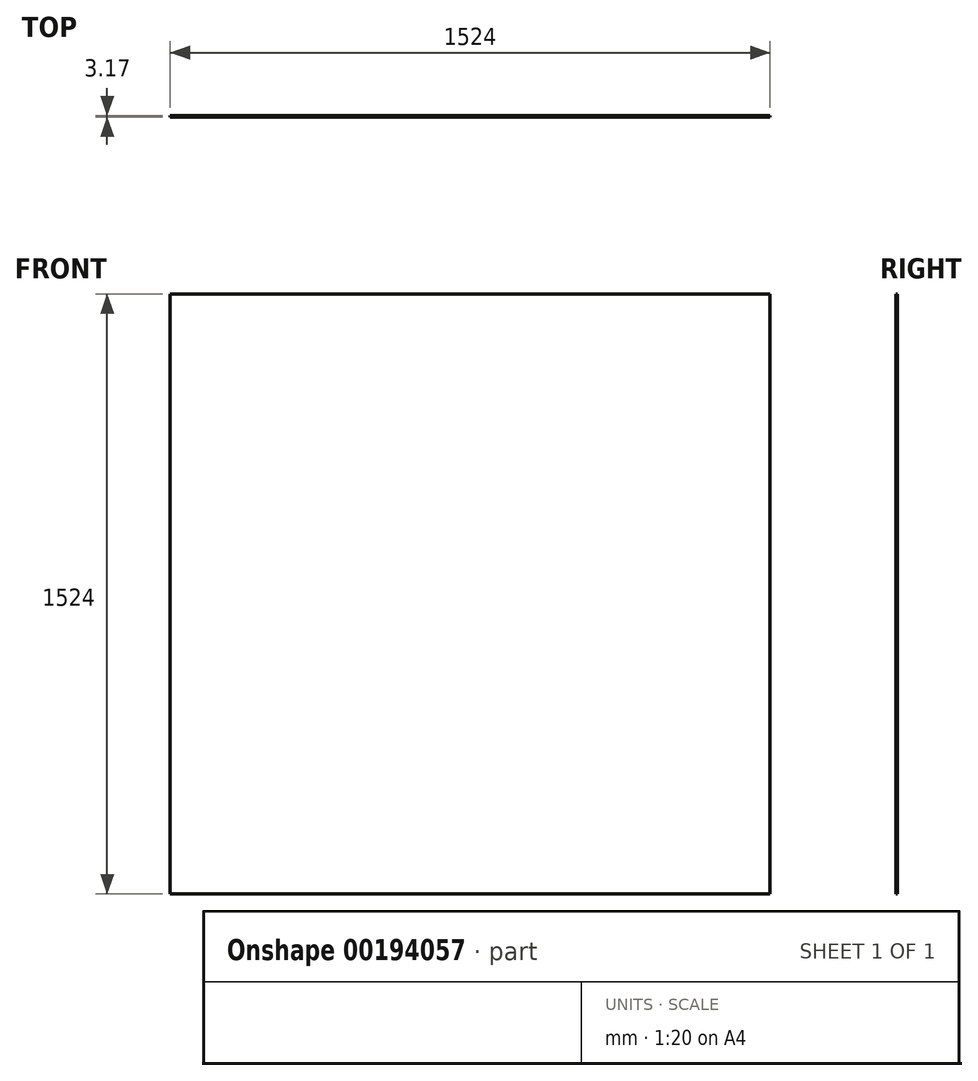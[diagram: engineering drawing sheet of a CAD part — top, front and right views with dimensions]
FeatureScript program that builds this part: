
annotation { "Feature Type Name" : "Feature", "Feature Type Description" : "" }
export const myFeature = defineFeature(function(context is Context, id is Id, definition is map)
    precondition{}
    {
        {
            var Q0;
            Q0=qCreatedBy(makeId("Front.planeOp"),FACE);
            var sketch = newSketch(context, id + "F0", { "sketchPlane" : qUnion([Q0])});
            skLineSegment(sketch, "E0.bottom", {"start": v(-825.5, 825.5) * mm, "end": v(825.5, 825.5) * mm});
            skLineSegment(sketch, "E0.top", {"start": v(-825.5, -825.5) * mm, "end": v(825.5, -825.5) * mm});
            skLineSegment(sketch, "E0.left", {"start": v(-825.5, 825.5) * mm, "end": v(-825.5, -825.5) * mm});
            skLineSegment(sketch, "E0.right", {"start": v(825.5, 825.5) * mm, "end": v(825.5, -825.5) * mm});
            skPoint(sketch, "E0.middle", {"position": v(0, 0) * mm});
            skSolve(sketch);
        }
        {
            var Q0;
            Q0=makeQuery(id+"F0.imprint","IMPRINT",FACE,{"disambiguationData":[TD([[makeQuery(id+"F0.imprint","IMPRINT",EDGE,{"derivedFrom":sQuery(id+"F0.wireOp",EDGE,"E0.bottom")}),-1.0]])]});
            extrude(context, id + "F1", {"entities" : qUnion([Q0]), "depth" : 3.17 * mm});
        }
        {
            var Q0;
            Q0=makeQuery(id+"F1.opExtrude","SWEPT_BODY",BODY,{"disambiguationData":[OSD([sQuery(id+"F0.wireOp",EDGE,"E0.bottom"),sQuery(id+"F0.wireOp",EDGE,"E0.top"),sQuery(id+"F0.wireOp",EDGE,"E0.left"),sQuery(id+"F0.wireOp",EDGE,"E0.right")])]});
            deleteBodies(context, id + "F2", {"entities" : qUnion([Q0])});
        }
        {
            var Q0;
            Q0=qCreatedBy(makeId("Front.planeOp"),FACE);
            var sketch = newSketch(context, id + "F3", { "sketchPlane" : qUnion([Q0])});
            skLineSegment(sketch, "E1.bottom", {"start": v(-762, -762) * mm, "end": v(762, -762) * mm});
            skLineSegment(sketch, "E1.top", {"start": v(-762, 762) * mm, "end": v(762, 762) * mm});
            skLineSegment(sketch, "E1.left", {"start": v(-762, -762) * mm, "end": v(-762, 762) * mm});
            skLineSegment(sketch, "E1.right", {"start": v(762, -762) * mm, "end": v(762, 762) * mm});
            skPoint(sketch, "E1.middle", {"position": v(0, 0) * mm});
            skSolve(sketch);
        }
        {
            var Q0;
            Q0=makeQuery(id+"F3.imprint","IMPRINT",FACE,{"disambiguationData":[TD([[makeQuery(id+"F3.imprint","IMPRINT",EDGE,{"derivedFrom":sQuery(id+"F3.wireOp",EDGE,"E1.bottom")}),1.0]])]});
            extrude(context, id + "F4", {"entities" : qUnion([Q0]), "depth" : 3.17 * mm});
        }
    });
